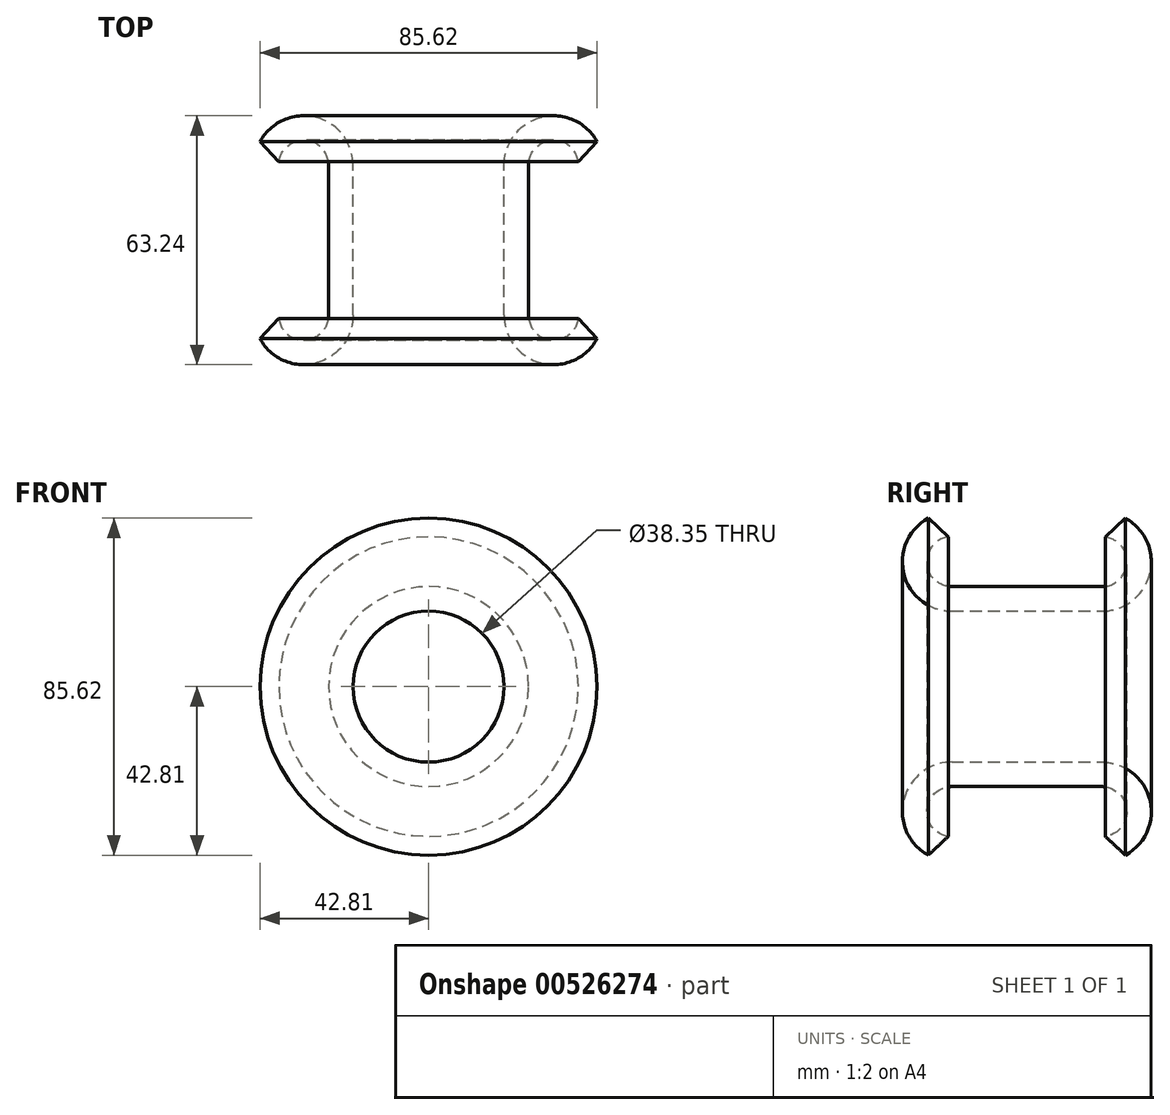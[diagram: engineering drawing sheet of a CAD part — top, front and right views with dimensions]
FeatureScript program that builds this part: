
annotation { "Feature Type Name" : "Feature", "Feature Type Description" : "" }
export const myFeature = defineFeature(function(context is Context, id is Id, definition is map)
    precondition{}
    {
        {
            var Q0;
            Q0=qCreatedBy(makeId("Front.planeOp"),FACE);
            var sketch = newSketch(context, id + "F0", { "sketchPlane" : qUnion([Q0])});
            skCircle(sketch, "E0", {"center": v(0, 0) * mm, "radius": 38.1 * mm});
            skSolve(sketch);
        }
        {
            var Q0;
            Q0=makeQuery(id+"F0.imprint","IMPRINT",FACE,{"disambiguationData":[TD([[makeQuery(id+"F0.imprint","IMPRINT",EDGE,{"derivedFrom":sQuery(id+"F0.wireOp",EDGE,"E0")}),1.0]])]});
            extrude(context, id + "F1", {"entities" : qUnion([Q0]), "depth" : 50.8 * mm, "offsetDistance" : 25.4 * mm});
        }
        {
            var Q0;
            Q0=makeQuery(id+"F1.opExtrude","CAP_FACE",FACE,{"disambiguationData":[OSD([sQuery(id+"F0.wireOp",EDGE,"E0")])],"isStart":true});
            var Q1;
            Q1=makeQuery(id+"F1.opExtrude","CAP_FACE",FACE,{"disambiguationData":[OSD([sQuery(id+"F0.wireOp",EDGE,"E0")])],"isStart":false});
            shell(context, id + "F2", {"entities" : qUnion([Q0, Q1]), "thickness" : 12.7 * mm});
        }
        {
            var Q0;
            Q0=makeQuery(id+"F1.opExtrude","SWEPT_FACE",FACE,{"disambiguationData":[OSD([sQuery(id+"F0.wireOp",EDGE,"E0")])]});
            var Q1;
            Q1=makeQuery(id+"F1.opExtrude","CAP_FACE",FACE,{"disambiguationData":[OSD([sQuery(id+"F0.wireOp",EDGE,"E0")])],"isStart":true});
            var Q2;
            Q2=makeQuery(id+"F1.opExtrude","CAP_FACE",FACE,{"disambiguationData":[OSD([sQuery(id+"F0.wireOp",EDGE,"E0")])],"isStart":false});
            fillet(context, id + "F3", {"entities" : qUnion([Q0, Q1, Q2]), "radius" : 6.35 * mm, "tangentPropagation" : true, "allowEdgeOverflow" : false});
        }
        {
            var Q0;
            Q0=makeQuery(id+"F1.opExtrude","SWEPT_FACE",FACE,{"disambiguationData":[OSD([sQuery(id+"F0.wireOp",EDGE,"E0")])]});
            shell(context, id + "F4", {"entities" : qUnion([Q0]), "thickness" : 6.22 * mm, "oppositeDirection" : true});
        }
        {
            var Q0;
            {var subQ0=sQuery(id+"F0.wireOp",EDGE,"E0");Q0=makeQuery(id+"F4.opShell","OFFSET_EDGE",EDGE,{"disambiguationData":[OSD([subQ0]),TDD([makeQuery(id+"F3.opFillet","BLEND_EDGE",EDGE,{"blendedFrom":[makeQuery(id+"F1.opExtrude","CAP_EDGE",EDGE,{"disambiguationData":[OSD([subQ0])],"isStart":false}),makeQuery(id+"F1.opExtrude","SWEPT_FACE",FACE,{"disambiguationData":[OSD([subQ0])]})],"blendedInto":[makeQuery(id+"F1.opExtrude","SWEPT_FACE",FACE,{"disambiguationData":[OSD([subQ0])]})]})]),OD(0.0)]});}
            var Q1;
            {var subQ0=sQuery(id+"F0.wireOp",EDGE,"E0");Q1=makeQuery(id+"F4.opShell","OFFSET_EDGE",EDGE,{"disambiguationData":[OSD([subQ0]),TDD([makeQuery(id+"F3.opFillet","BLEND_EDGE",EDGE,{"blendedFrom":[makeQuery(id+"F1.opExtrude","CAP_EDGE",EDGE,{"disambiguationData":[OSD([subQ0])],"isStart":true}),makeQuery(id+"F1.opExtrude","SWEPT_FACE",FACE,{"disambiguationData":[OSD([subQ0])]})],"blendedInto":[makeQuery(id+"F1.opExtrude","SWEPT_FACE",FACE,{"disambiguationData":[OSD([subQ0])]})]})]),OD(0.0)]});}
            chamfer(context, id + "F5", {"entities" : qUnion([Q0, Q1]), "chamferType" : ChamferType.OFFSET_ANGLE, "width" : 6.35 * mm, "oppositeDirection" : false, "angle" : 25 * degree, "tangentPropagation" : true});
        }
    });
